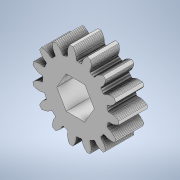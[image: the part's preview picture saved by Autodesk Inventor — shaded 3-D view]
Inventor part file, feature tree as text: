
AUTODESK INVENTOR PART (.ipt)
format: ipt  version: 2022 (Build 260153000, 153)  size: 3,004,416 bytes
history: native  units: mm
features: sketch x2, extrude x2
ambient origin geometry x8: Origin, YZ Plane, XZ Plane, XY Plane, X Axis, Y Axis, Z Axis, Center Point
bodies: Solid1 (feature_tree)
feature tree (4):
  sketch  "Sketch1"  dims[d2=5.55mm d3=0.0mm d34=3.1mm]
  extrude  "Extrusion2"  Depth=5.55mm
  extrude  "Extrusion7"  Depth=10.0mm
  sketch  "Sketch6"  dims[d35=60.0mm d37=360.0deg d39=0.5mm d40=10.0mm d41=0.0mm]
